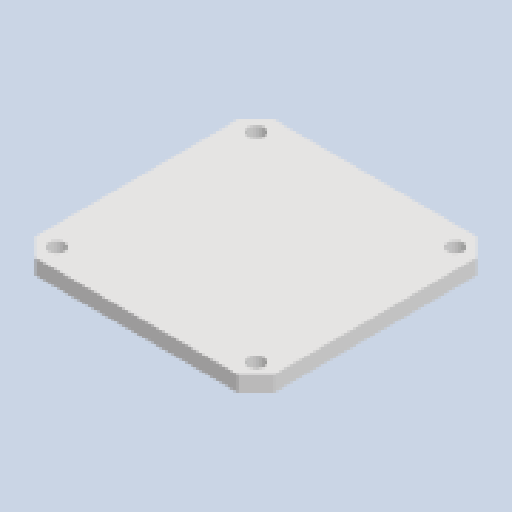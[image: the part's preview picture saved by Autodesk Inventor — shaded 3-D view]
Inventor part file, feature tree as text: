
AUTODESK INVENTOR PART (.ipt)
format: ipt  version: 2025.2 (Build 292293000, 293)  size: 107,520 bytes
history: native  units: mm
features: sketch x2, extrude x1, hole x1
ambient origin geometry x8: Origin, YZ Plane, XZ Plane, XY Plane, X Axis, Y Axis, Z Axis, Center Point
bodies: Solid1 (feature_tree)
feature tree (4):
  sketch  "Sketch1"  dims[d0=51.657mm d1=51.657mm]
  extrude  "Extrusion1"  Depth=51.657mm
  hole  "Hole1"  [1 undecoded]
  sketch  "Sketch Circular Pattern1"  dims[d4=31.0mm d5=4.0mm d6=40.0mm d8=360.0deg d10=4.0mm d11=0.0mm d12=4.2mm d13=6.0mm d14=4.0mm d15=2.0mm d16=90.0deg d17=8.0mm d18=20.594885mm]
note: 1 required parameter value undecoded (feature->parameter linkage not recoverable at this tier; creation-order binding heuristic only, values carry confidence <= 0.55)
